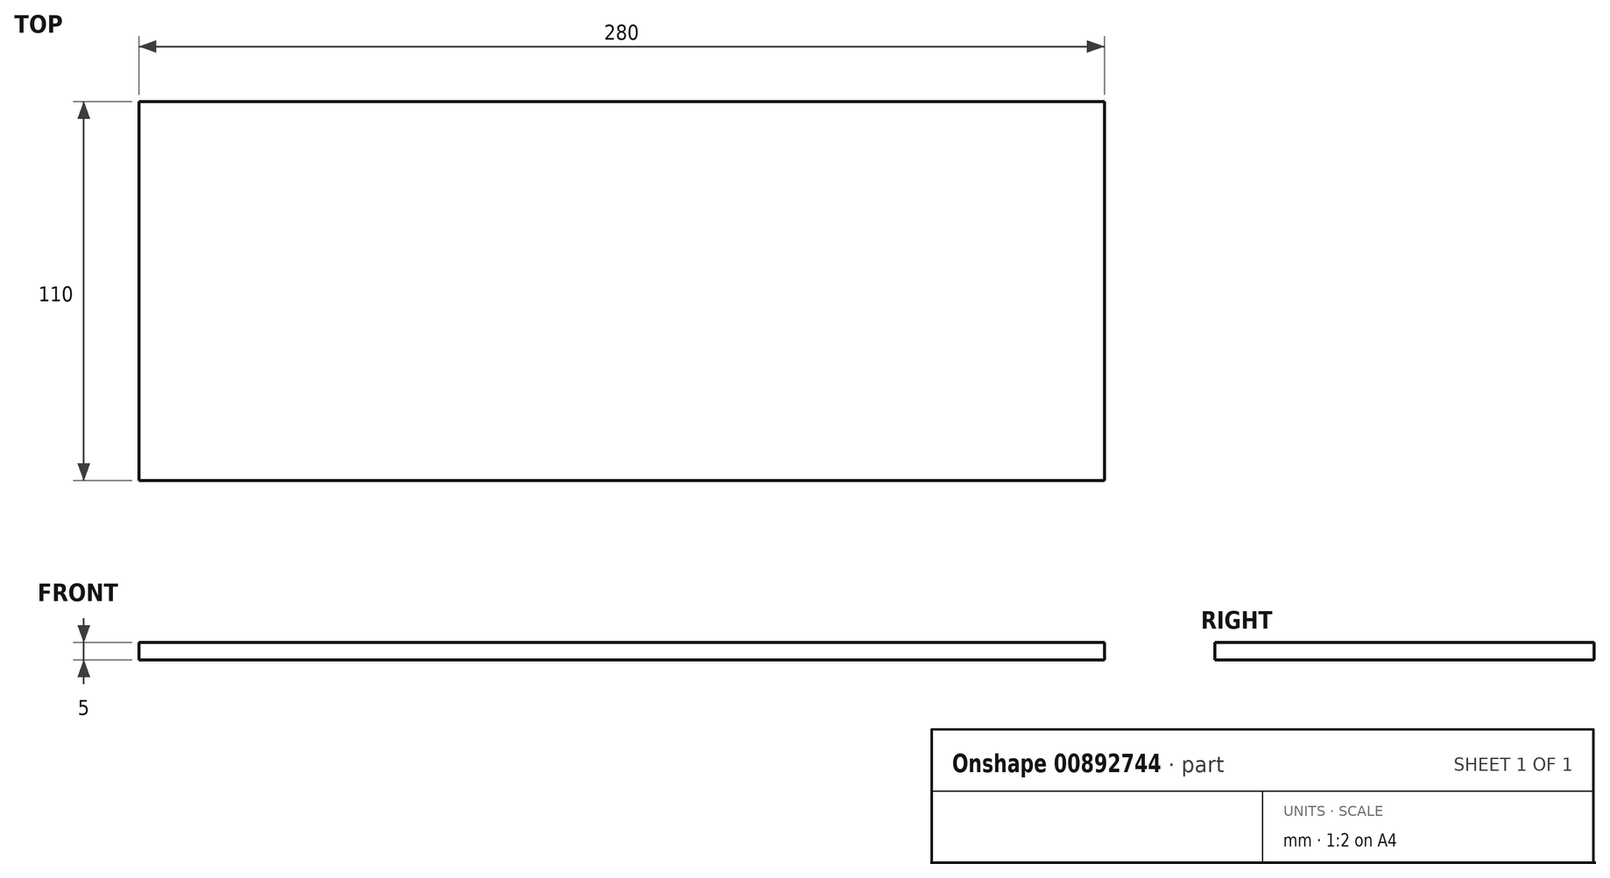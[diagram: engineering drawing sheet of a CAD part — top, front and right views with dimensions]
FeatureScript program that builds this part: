
annotation { "Feature Type Name" : "Feature", "Feature Type Description" : "" }
export const myFeature = defineFeature(function(context is Context, id is Id, definition is map)
    precondition{}
    {
        {
            var Q0;
            Q0=qCreatedBy(makeId("Top.planeOp"),FACE);
            var sketch = newSketch(context, id + "F0", { "sketchPlane" : qUnion([Q0])});
            skLineSegment(sketch, "E0.bottom", {"start": v(140, 55) * mm, "end": v(-140, 55) * mm});
            skLineSegment(sketch, "E0.top", {"start": v(140, -55) * mm, "end": v(-140, -55) * mm});
            skLineSegment(sketch, "E0.left", {"start": v(140, 55) * mm, "end": v(140, -55) * mm});
            skLineSegment(sketch, "E0.right", {"start": v(-140, 55) * mm, "end": v(-140, -55) * mm});
            skPoint(sketch, "E0.middle", {"position": v(0, 0) * mm});
            skSolve(sketch);
        }
        {
            var Q0;
            Q0=makeQuery(id+"F0.imprint","IMPRINT",FACE,{"disambiguationData":[TD([[makeQuery(id+"F0.imprint","IMPRINT",EDGE,{"derivedFrom":sQuery(id+"F0.wireOp",EDGE,"E0.bottom")}),1.0]])]});
            extrude(context, id + "F1", {"entities" : qUnion([Q0]), "depth" : 5 * mm, "offsetDistance" : 25 * mm});
        }
    });
